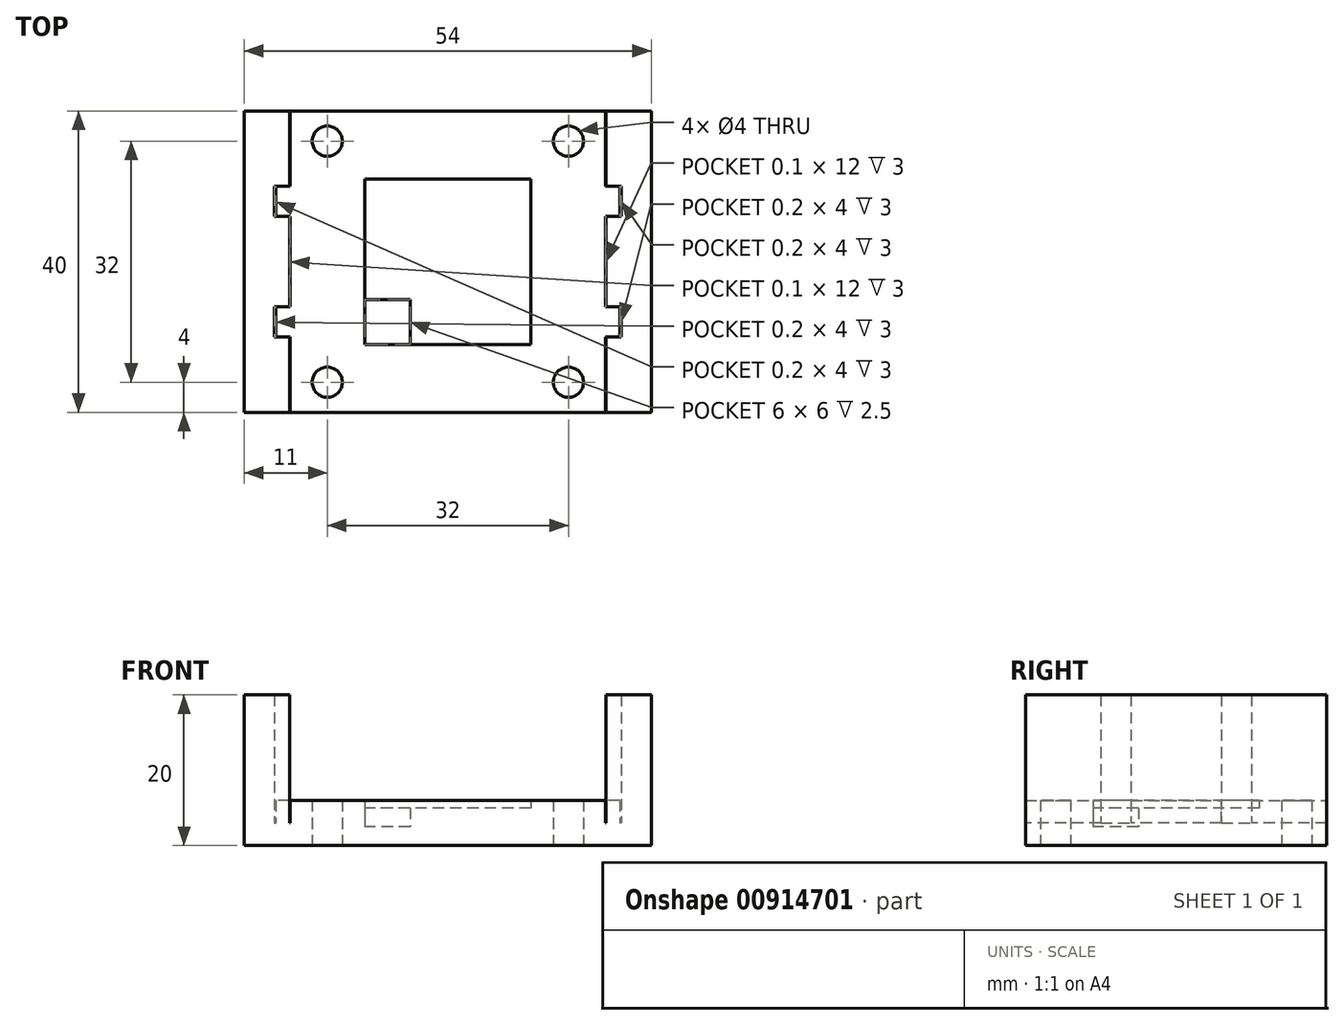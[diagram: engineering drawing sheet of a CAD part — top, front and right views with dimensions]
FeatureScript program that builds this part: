
annotation { "Feature Type Name" : "Feature", "Feature Type Description" : "" }
export const myFeature = defineFeature(function(context is Context, id is Id, definition is map)
    precondition{}
    {
        {
            var Q0;
            Q0=qCreatedBy(makeId("Top.planeOp"),FACE);
            var sketch = newSketch(context, id + "F0", { "sketchPlane" : qUnion([Q0])});
            skCircle(sketch, "E0", {"center": v(-4, 4) * mm, "radius": 3 * mm});
            skCircle(sketch, "E1", {"center": v(4, 4) * mm, "radius": 3 * mm});
            skCircle(sketch, "E2", {"center": v(4, -4) * mm, "radius": 3 * mm});
            skCircle(sketch, "E3", {"center": v(-4, -4) * mm, "radius": 3 * mm});
            skLineSegment(sketch, "E4.bottom", {"start": v(27, -20) * mm, "end": v(-27, -20) * mm});
            skLineSegment(sketch, "E4.top", {"start": v(27, 20) * mm, "end": v(-27, 20) * mm});
            skLineSegment(sketch, "E4.left", {"start": v(27, -20) * mm, "end": v(27, 20) * mm});
            skLineSegment(sketch, "E4.right", {"start": v(-27, -20) * mm, "end": v(-27, 20) * mm});
            skPoint(sketch, "E4.middle", {"position": v(0, 0) * mm});
            skCircle(sketch, "E5", {"center": v(16, -16) * mm, "radius": 2 * mm});
            skCircle(sketch, "E6", {"center": v(-16, -16) * mm, "radius": 2 * mm});
            skCircle(sketch, "E7", {"center": v(-16, 16) * mm, "radius": 2 * mm});
            skCircle(sketch, "E8", {"center": v(16, 16) * mm, "radius": 2 * mm});
            skSolve(sketch);
        }
        {
            var Q0;
            Q0 = qSketchRegion(id + "F0", true);
            extrude(context, id + "F1", {"entities" : qUnion([Q0]), "depth" : 3 * mm, "offsetDistance" : 25 * mm});
        }
        {
            var Q0;
            Q0=qCreatedBy(makeId("Top.planeOp"),FACE);
            var sketch = newSketch(context, id + "F2", { "sketchPlane" : qUnion([Q0])});
            skPoint(sketch, "E9.middle", {"position": v(0, 0) * mm});
            skLineSegment(sketch, "E10.right", {"start": v(-27, -20) * mm, "end": v(-27, 12.5) * mm});
            skLineSegment(sketch, "E11.bottom", {"start": v(21, 20) * mm, "end": v(27, 20) * mm});
            skLineSegment(sketch, "E11.top", {"start": v(21, -20) * mm, "end": v(27, -20) * mm});
            skLineSegment(sketch, "E11.left", {"start": v(27, 20) * mm, "end": v(27, -20) * mm});
            skLineSegment(sketch, "E11.right", {"start": v(21, 20) * mm, "end": v(21, 10) * mm});
            skLineSegment(sketch, "E12.bottom", {"start": v(-27, 20) * mm, "end": v(-21, 20) * mm});
            skLineSegment(sketch, "E12.top", {"start": v(-27, -20) * mm, "end": v(-21, -20) * mm});
            skLineSegment(sketch, "E12.left", {"start": v(-21, 20) * mm, "end": v(-21, 10) * mm});
            skLineSegment(sketch, "E12.right", {"start": v(-27, 20) * mm, "end": v(-27, -20) * mm});
            skLineSegment(sketch, "E13.bottom", {"start": v(-21, 10) * mm, "end": v(-23, 10) * mm});
            skLineSegment(sketch, "E13.top", {"start": v(-21, 6) * mm, "end": v(-23, 6) * mm});
            skLineSegment(sketch, "E13.right", {"start": v(-23, 10) * mm, "end": v(-23, 6) * mm});
            skLineSegment(sketch, "E14.bottom", {"start": v(-21, -6) * mm, "end": v(-23, -6) * mm});
            skLineSegment(sketch, "E14.top", {"start": v(-21, -10) * mm, "end": v(-23, -10) * mm});
            skLineSegment(sketch, "E14.right", {"start": v(-23, -6) * mm, "end": v(-23, -10) * mm});
            skLineSegment(sketch, "E15.trimOffspring", {"start": v(-21, 6) * mm, "end": v(-21, -6) * mm});
            skLineSegment(sketch, "E16.trimOffspring", {"start": v(-21, -10) * mm, "end": v(-21, -20) * mm});
            skLineSegment(sketch, "E17.bottom", {"start": v(21, 10) * mm, "end": v(23, 10) * mm});
            skLineSegment(sketch, "E17.top", {"start": v(21, 6) * mm, "end": v(23, 6) * mm});
            skLineSegment(sketch, "E17.right", {"start": v(23, 10) * mm, "end": v(23, 6) * mm});
            skLineSegment(sketch, "E18.bottom", {"start": v(21, -6) * mm, "end": v(23, -6) * mm});
            skLineSegment(sketch, "E18.top", {"start": v(21, -10) * mm, "end": v(23, -10) * mm});
            skLineSegment(sketch, "E18.right", {"start": v(23, -6) * mm, "end": v(23, -10) * mm});
            skLineSegment(sketch, "E19.trimOffspring", {"start": v(21, 6) * mm, "end": v(21, -6) * mm});
            skLineSegment(sketch, "E20.trimOffspring", {"start": v(21, -10) * mm, "end": v(21, -20) * mm});
            skSolve(sketch);
        }
        {
            var Q0;
            Q0 = qSketchRegion(id + "F2", true);
            extrude(context, id + "F3", {"entities" : qUnion([Q0]), "operationType" : NewBodyOperationType.ADD, "depth" : 20 * mm, "offsetDistance" : 25 * mm});
        }
        {
            var Q0;
            Q0=qCreatedBy(makeId("Top.planeOp"),FACE);
            var sketch = newSketch(context, id + "F4", { "sketchPlane" : qUnion([Q0])});
            skLineSegment(sketch, "E21.bottom", {"start": v(20.9, -20) * mm, "end": v(-20.9, -20) * mm});
            skLineSegment(sketch, "E21.top", {"start": v(20.9, 20) * mm, "end": v(-20.9, 20) * mm});
            skLineSegment(sketch, "E21.left", {"start": v(20.9, -20) * mm, "end": v(20.9, 20) * mm});
            skLineSegment(sketch, "E21.right", {"start": v(-20.9, -20) * mm, "end": v(-20.9, 20) * mm});
            skPoint(sketch, "E21.middle", {"position": v(0, 0) * mm});
            skSolve(sketch);
        }
        {
            var Q0;
            Q0 = qSketchRegion(id + "F4", true);
            extrude(context, id + "F5", {"entities" : qUnion([Q0]), "depth" : 6 * mm, "offsetDistance" : 25 * mm});
        }
        {
            var Q0;
            Q0=qCreatedBy(makeId("Top.planeOp"),FACE);
            var sketch = newSketch(context, id + "F6", { "sketchPlane" : qUnion([Q0])});
            skLineSegment(sketch, "E22.bottom", {"start": v(11, 11) * mm, "end": v(-11, 11) * mm});
            skLineSegment(sketch, "E22.top", {"start": v(11, -11) * mm, "end": v(-11, -11) * mm});
            skLineSegment(sketch, "E22.left", {"start": v(11, 11) * mm, "end": v(11, -11) * mm});
            skLineSegment(sketch, "E22.right", {"start": v(-11, 11) * mm, "end": v(-11, -11) * mm});
            skPoint(sketch, "E22.middle", {"position": v(0, 0) * mm});
            skSolve(sketch);
        }
        {
            var Q0;
            Q0 = qSketchRegion(id + "F6", true);
            extrude(context, id + "F7", {"entities" : qUnion([Q0]), "operationType" : NewBodyOperationType.REMOVE, "depth" : 6 * mm, "offsetDistance" : 25 * mm, "hasSecondDirection" : true, "secondDirectionOppositeDirection" : false, "secondDirectionDepth" : 5 * mm});
        }
        {
            var Q0;
            Q0=qCreatedBy(makeId("Top.planeOp"),FACE);
            var sketch = newSketch(context, id + "F8", { "sketchPlane" : qUnion([Q0])});
            skLineSegment(sketch, "E23.bottom", {"start": v(-5, -5) * mm, "end": v(-11, -5) * mm});
            skLineSegment(sketch, "E23.top", {"start": v(-5, -11) * mm, "end": v(-11, -11) * mm});
            skLineSegment(sketch, "E23.left", {"start": v(-5, -5) * mm, "end": v(-5, -11) * mm});
            skLineSegment(sketch, "E23.right", {"start": v(-11, -5) * mm, "end": v(-11, -11) * mm});
            skSolve(sketch);
        }
        {
            var Q0;
            Q0 = qSketchRegion(id + "F8", true);
            extrude(context, id + "F9", {"entities" : qUnion([Q0]), "operationType" : NewBodyOperationType.REMOVE, "depth" : 5 * mm, "offsetDistance" : 25 * mm, "hasSecondDirection" : true, "secondDirectionOppositeDirection" : false, "secondDirectionDepth" : 2.5 * mm});
        }
        {
            var Q0;
            Q0=qCreatedBy(makeId("Top.planeOp"),FACE);
            var sketch = newSketch(context, id + "F10", { "sketchPlane" : qUnion([Q0])});
            skLineSegment(sketch, "E24.bottom", {"start": v(-16.3, 8.45) * mm, "end": v(-12.5, 8.45) * mm});
            skLineSegment(sketch, "E24.top", {"start": v(-16.3, 6.55) * mm, "end": v(-12.5, 6.55) * mm});
            skLineSegment(sketch, "E24.left", {"start": v(-16.3, 8.45) * mm, "end": v(-16.3, 6.55) * mm});
            skLineSegment(sketch, "E24.right", {"start": v(-12.5, 8.45) * mm, "end": v(-12.5, 6.55) * mm});
            skLineSegment(sketch, "E25.bottom", {"start": v(-16.3, -6.55) * mm, "end": v(-12.5, -6.55) * mm});
            skLineSegment(sketch, "E25.top", {"start": v(-16.3, -8.45) * mm, "end": v(-12.5, -8.45) * mm});
            skLineSegment(sketch, "E25.left", {"start": v(-16.3, -6.55) * mm, "end": v(-16.3, -8.45) * mm});
            skLineSegment(sketch, "E25.right", {"start": v(-12.5, -6.55) * mm, "end": v(-12.5, -8.45) * mm});
            skLineSegment(sketch, "E26.bottom", {"start": v(12.5, 8.45) * mm, "end": v(16.3, 8.45) * mm});
            skLineSegment(sketch, "E26.top", {"start": v(12.5, 6.55) * mm, "end": v(16.3, 6.55) * mm});
            skLineSegment(sketch, "E26.left", {"start": v(12.5, 8.45) * mm, "end": v(12.5, 6.55) * mm});
            skLineSegment(sketch, "E26.right", {"start": v(16.3, 8.45) * mm, "end": v(16.3, 6.55) * mm});
            skLineSegment(sketch, "E27.bottom", {"start": v(12.5, -6.55) * mm, "end": v(16.3, -6.55) * mm});
            skLineSegment(sketch, "E27.top", {"start": v(12.5, -8.45) * mm, "end": v(16.3, -8.45) * mm});
            skLineSegment(sketch, "E27.left", {"start": v(12.5, -6.55) * mm, "end": v(12.5, -8.45) * mm});
            skLineSegment(sketch, "E27.right", {"start": v(16.3, -6.55) * mm, "end": v(16.3, -8.45) * mm});
            skSolve(sketch);
        }
        {
            var Q0;
            Q0 = qSketchRegion(id + "F10", true);
            extrude(context, id + "F11", {"entities" : qUnion([Q0]), "operationType" : NewBodyOperationType.ADD, "depth" : 5 * mm, "offsetDistance" : 25 * mm});
        }
        {
            var Q0;
            Q0=qCreatedBy(makeId("Top.planeOp"),FACE);
            var sketch = newSketch(context, id + "F12", { "sketchPlane" : qUnion([Q0])});
            skCircle(sketch, "E28", {"center": v(-16, 16) * mm, "radius": 2 * mm});
            skCircle(sketch, "E29", {"center": v(16, 16) * mm, "radius": 2 * mm});
            skCircle(sketch, "E30", {"center": v(16, -16) * mm, "radius": 2 * mm});
            skCircle(sketch, "E31", {"center": v(-16, -16) * mm, "radius": 2 * mm});
            skSolve(sketch);
        }
        {
            var Q0;
            Q0 = qSketchRegion(id + "F12", true);
            extrude(context, id + "F13", {"entities" : qUnion([Q0]), "operationType" : NewBodyOperationType.REMOVE, "depth" : 25 * mm, "offsetDistance" : 25 * mm});
        }
        {
            var Q0;
            Q0=qCreatedBy(makeId("Top.planeOp"),FACE);
            var sketch = newSketch(context, id + "F14", { "sketchPlane" : qUnion([Q0])});
            skLineSegment(sketch, "E32.bottom", {"start": v(-20.8, 10) * mm, "end": v(-22.8, 10) * mm});
            skLineSegment(sketch, "E32.top", {"start": v(-20.8, 6) * mm, "end": v(-22.8, 6) * mm});
            skLineSegment(sketch, "E32.left", {"start": v(-20.8, 10) * mm, "end": v(-20.8, 6) * mm});
            skLineSegment(sketch, "E32.right", {"start": v(-22.8, 10) * mm, "end": v(-22.8, 6) * mm});
            skLineSegment(sketch, "E33.bottom", {"start": v(-20.8, -6) * mm, "end": v(-22.8, -6) * mm});
            skLineSegment(sketch, "E33.top", {"start": v(-20.8, -10) * mm, "end": v(-22.8, -10) * mm});
            skLineSegment(sketch, "E33.left", {"start": v(-20.8, -6) * mm, "end": v(-20.8, -10) * mm});
            skLineSegment(sketch, "E33.right", {"start": v(-22.8, -6) * mm, "end": v(-22.8, -10) * mm});
            skLineSegment(sketch, "E34.bottom", {"start": v(22.8, 10) * mm, "end": v(20.8, 10) * mm});
            skLineSegment(sketch, "E34.top", {"start": v(22.8, 6) * mm, "end": v(20.8, 6) * mm});
            skLineSegment(sketch, "E34.left", {"start": v(22.8, 10) * mm, "end": v(22.8, 6) * mm});
            skLineSegment(sketch, "E34.right", {"start": v(20.8, 10) * mm, "end": v(20.8, 6) * mm});
            skLineSegment(sketch, "E35.bottom", {"start": v(22.8, -6) * mm, "end": v(20.8, -6) * mm});
            skLineSegment(sketch, "E35.top", {"start": v(22.8, -10) * mm, "end": v(20.8, -10) * mm});
            skLineSegment(sketch, "E35.left", {"start": v(22.8, -6) * mm, "end": v(22.8, -10) * mm});
            skLineSegment(sketch, "E35.right", {"start": v(20.8, -6) * mm, "end": v(20.8, -10) * mm});
            skSolve(sketch);
        }
        {
            var Q0;
            Q0 = qSketchRegion(id + "F14", true);
            extrude(context, id + "F15", {"entities" : qUnion([Q0]), "operationType" : NewBodyOperationType.ADD, "depth" : 6 * mm, "offsetDistance" : 25 * mm});
        }
    });
